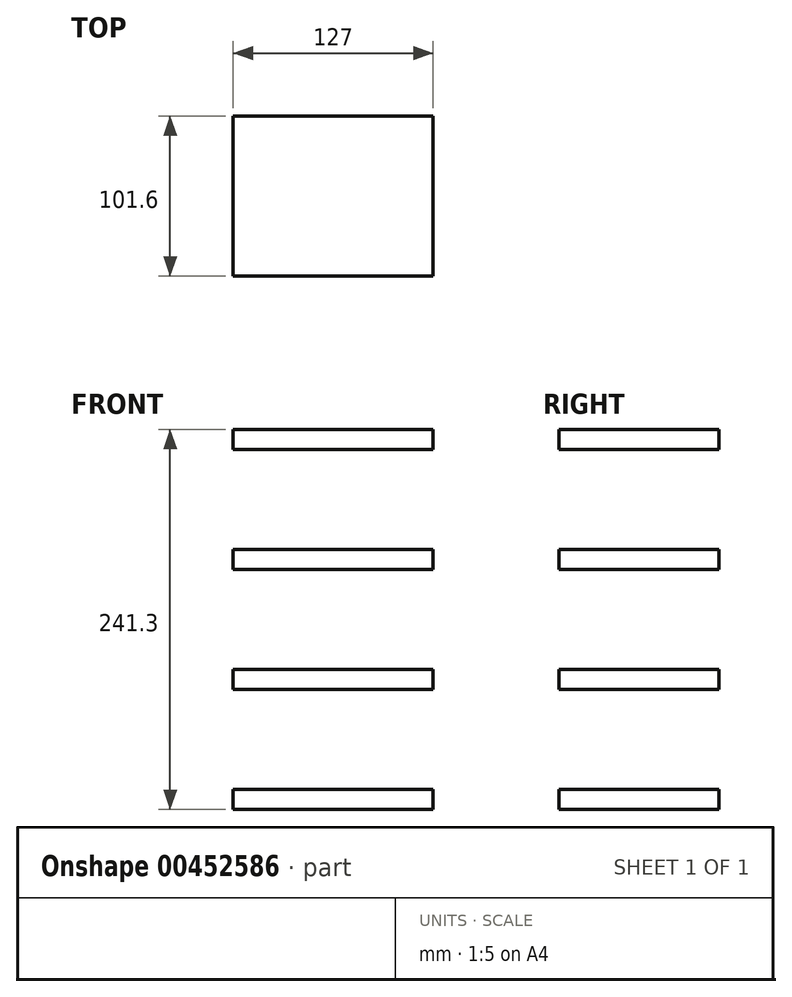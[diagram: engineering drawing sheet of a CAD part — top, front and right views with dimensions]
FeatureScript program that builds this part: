
annotation { "Feature Type Name" : "Feature", "Feature Type Description" : "" }
export const myFeature = defineFeature(function(context is Context, id is Id, definition is map)
    precondition{}
    {
        {
            var Q0;
            Q0=qCreatedBy(makeId("Front.planeOp"),FACE);
            var sketch = newSketch(context, id + "F0", { "sketchPlane" : qUnion([Q0])});
            skLineSegment(sketch, "E0.bottom", {"start": v(63.5, 6.35) * mm, "end": v(-63.5, 6.35) * mm});
            skLineSegment(sketch, "E0.top", {"start": v(63.5, -6.35) * mm, "end": v(-63.5, -6.35) * mm});
            skLineSegment(sketch, "E0.left", {"start": v(63.5, 6.35) * mm, "end": v(63.5, -6.35) * mm});
            skLineSegment(sketch, "E0.right", {"start": v(-63.5, 6.35) * mm, "end": v(-63.5, -6.35) * mm});
            skPoint(sketch, "E0.middle", {"position": v(0, 0) * mm});
            skLineSegment(sketch, "E1.bottom", {"start": v(-63.5, 69.85) * mm, "end": v(63.5, 69.85) * mm});
            skLineSegment(sketch, "E1.top", {"start": v(-63.5, 82.55) * mm, "end": v(63.5, 82.55) * mm});
            skLineSegment(sketch, "E1.left", {"start": v(-63.5, 69.85) * mm, "end": v(-63.5, 82.55) * mm});
            skLineSegment(sketch, "E1.right", {"start": v(63.5, 69.85) * mm, "end": v(63.5, 82.55) * mm});
            skPoint(sketch, "E1.middle", {"position": v(0, 76.2) * mm});
            skLineSegment(sketch, "E2.bottom", {"start": v(-63.5, -69.85) * mm, "end": v(63.5, -69.85) * mm});
            skLineSegment(sketch, "E2.top", {"start": v(-63.5, -82.55) * mm, "end": v(63.5, -82.55) * mm});
            skLineSegment(sketch, "E2.left", {"start": v(-63.5, -69.85) * mm, "end": v(-63.5, -82.55) * mm});
            skLineSegment(sketch, "E2.right", {"start": v(63.5, -69.85) * mm, "end": v(63.5, -82.55) * mm});
            skPoint(sketch, "E2.middle", {"position": v(0, -76.2) * mm});
            skLineSegment(sketch, "E3.bottom", {"start": v(-63.5, -158.75) * mm, "end": v(63.5, -158.75) * mm});
            skLineSegment(sketch, "E3.top", {"start": v(-63.5, -146.05) * mm, "end": v(63.5, -146.05) * mm});
            skLineSegment(sketch, "E3.left", {"start": v(-63.5, -158.75) * mm, "end": v(-63.5, -146.05) * mm});
            skLineSegment(sketch, "E3.right", {"start": v(63.5, -158.75) * mm, "end": v(63.5, -146.05) * mm});
            skPoint(sketch, "E3.middle", {"position": v(0, -152.4) * mm});
            skSolve(sketch);
        }
        {
            var Q0;
            Q0=makeQuery(id+"F0.imprint","IMPRINT",FACE,{"disambiguationData":[TD([[makeQuery(id+"F0.imprint","IMPRINT",EDGE,{"derivedFrom":sQuery(id+"F0.wireOp",EDGE,"E1.bottom")}),1.0]])]});
            var Q1;
            Q1=makeQuery(id+"F0.imprint","IMPRINT",FACE,{"disambiguationData":[TD([[makeQuery(id+"F0.imprint","IMPRINT",EDGE,{"derivedFrom":sQuery(id+"F0.wireOp",EDGE,"E0.bottom")}),1.0]])]});
            var Q2;
            Q2=makeQuery(id+"F0.imprint","IMPRINT",FACE,{"disambiguationData":[TD([[makeQuery(id+"F0.imprint","IMPRINT",EDGE,{"derivedFrom":sQuery(id+"F0.wireOp",EDGE,"E2.bottom")}),-1.0]])]});
            var Q3;
            Q3=makeQuery(id+"F0.imprint","IMPRINT",FACE,{"disambiguationData":[TD([[makeQuery(id+"F0.imprint","IMPRINT",EDGE,{"derivedFrom":sQuery(id+"F0.wireOp",EDGE,"E3.bottom")}),1.0]])]});
            extrude(context, id + "F1", {"entities" : qUnion([Q0, Q1, Q2, Q3]), "endBound" : BoundingType.SYMMETRIC, "depth" : 101.6 * mm});
        }
        {
            var Q0;
            Q0=makeQuery(id+"F1.opExtrude","SWEPT_FACE",FACE,{"disambiguationData":[OSD([sQuery(id+"F0.wireOp",EDGE,"E1.top")])]});
            var sketch = newSketch(context, id + "F2", { "sketchPlane" : qUnion([Q0])});
            skCircle(sketch, "E4", {"center": v(50.8, -38.1) * mm, "radius": 3.81 * mm});
            skCircle(sketch, "E5", {"center": v(50.8, 38.1) * mm, "radius": 3.81 * mm});
            skCircle(sketch, "E6", {"center": v(-50.8, 38.1) * mm, "radius": 3.81 * mm});
            skCircle(sketch, "E7", {"center": v(-50.8, -38.1) * mm, "radius": 3.81 * mm});
            skSolve(sketch);
        }
        {
            var Q0;
            Q0=sQuery(id+"F2.wireOp",EDGE,"E4");
            var Q1;
            Q1=sQuery(id+"F2.wireOp",EDGE,"E5");
            var Q2;
            Q2=sQuery(id+"F2.wireOp",EDGE,"E6");
            var Q3;
            Q3=sQuery(id+"F2.wireOp",EDGE,"E7");
            var Q4;
            Q4=makeQuery(id+"F1.opExtrude","SWEPT_FACE",FACE,{"disambiguationData":[OSD([sQuery(id+"F0.wireOp",EDGE,"E3.bottom")])]});
            extrude(context, id + "F3", {"bodyType" : ToolBodyType.SURFACE, "surfaceEntities" : qUnion([Q0, Q1, Q2, Q3]), "oppositeDirection" : true, "endBoundEntityFace" : qUnion([Q4]), "depth" : 254 * mm, "hasSecondDirection" : true, "secondDirectionOppositeDirection" : true, "secondDirectionDepth" : -12.7 * mm});
        }
    });
